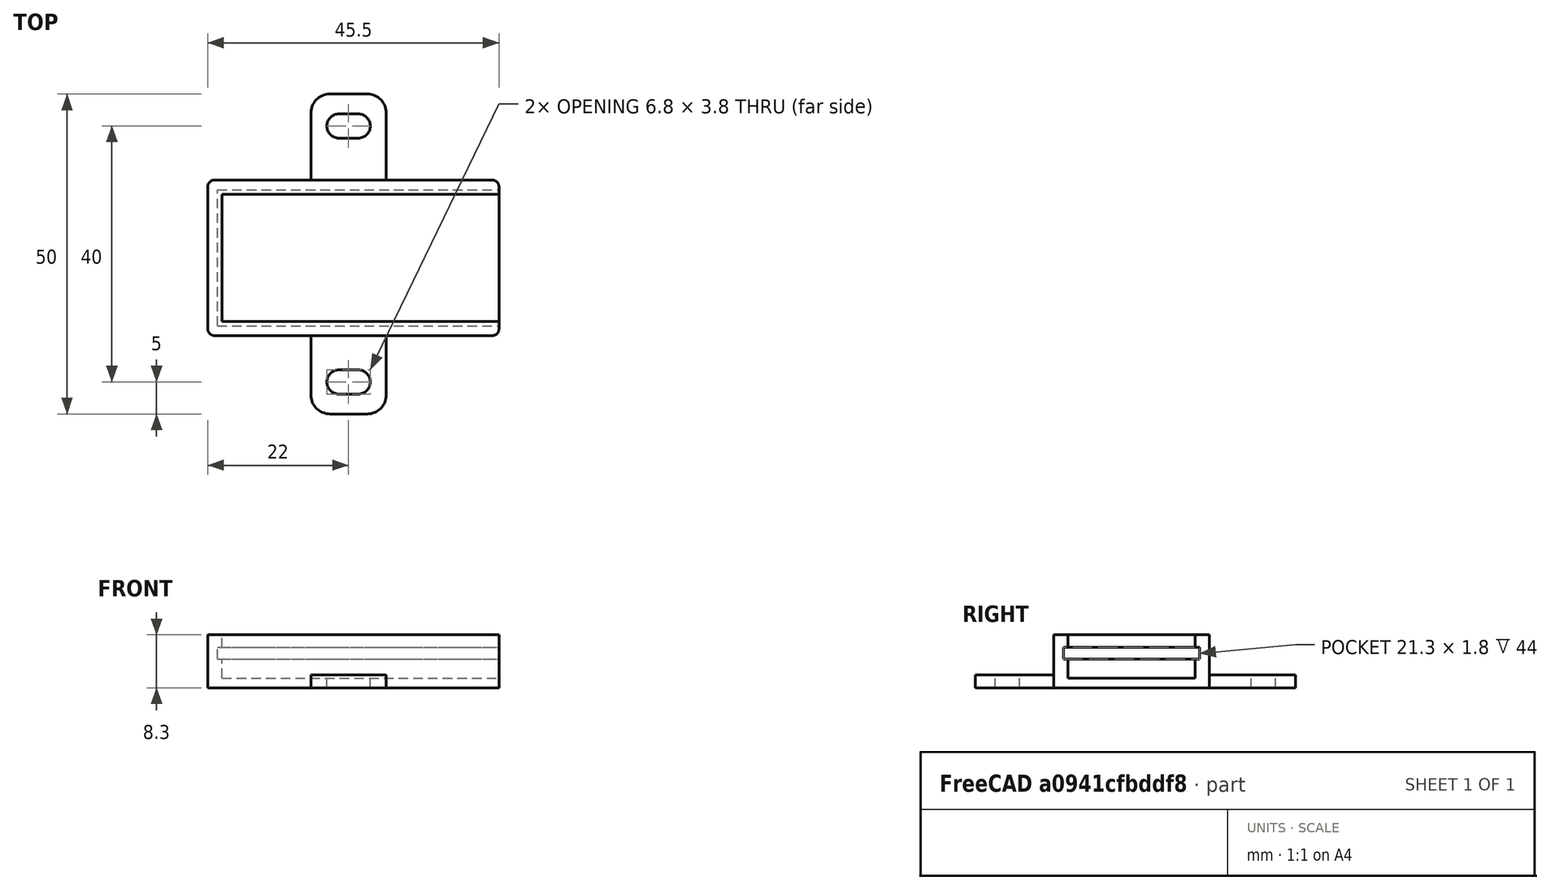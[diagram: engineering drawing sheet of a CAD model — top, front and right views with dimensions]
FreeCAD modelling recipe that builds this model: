
FCSTD DOCUMENT  (FreeCAD 0.19R)
Label: step_down_lm2596s_44x21
License: FreeArt
LicenseURL: http://artlibre.org/licence/lal
objects: Part::Box×3, Part::MultiFuse×2, Spreadsheet::Sheet×1, Part::Fillet×1, Part::Feature×1, Part::Cut×1, App::Part×1
note: 8 computed .brp shape members not serialized (recipe doc carries the construction recipe); baked Part::Feature solids carry a one-line shape summary decoded from their .brp

FEATURE [Spreadsheet::Sheet] Spreadsheet  label="p"
  cells = A1=pcb_x; B1(pcb_x)=44; A2=pcb_y; B2(pcb_y)=21.3; A3=pcb_z; B3(pcb_z)=1.8; A4=pcb_under; B4(pcb_under)=3; A5=side_wall; B5(side_wall)=1.5; A6=pcb_side_lane; B6(pcb_side_lane)=0.7; A7=bottom_wall; B7(bottom_wall)=1.5; A8=pcb_above; B8(pcb_above)=2
FEATURE [Part::Box] Box  label="external cube"
  AttacherType = Attacher::AttachEngine3D
  Height = 8.3
  Length = 45.5
  Width = 24.3
  expr: Length = <<p>>.pcb_x + <<p>>.side_wall
  expr: Width = <<p>>.pcb_y + 2 * <<p>>.side_wall
  expr: Height = <<p>>.bottom_wall + <<p>>.pcb_under + <<p>>.pcb_z + <<p>>.pcb_above
FEATURE [Part::Box] Box006  label="internal cube"
  AttacherType = Attacher::AttachEngine3D
  Height = 6.8
  Length = 44.1
  Placement = pos=(2.2,2.2,1.5) rot=(0,0,1;0rad)
  Width = 19.9
  expr: Length = <<p>>.pcb_x - 2 * <<p>>.pcb_side_lane + <<p>>.side_wall
  expr: Width = <<p>>.pcb_y - 2 * <<p>>.pcb_side_lane
  expr: Height = <<p>>.pcb_under + <<p>>.pcb_z + <<p>>.pcb_above
  expr: .Placement.Base.z = <<p>>.bottom_wall
  expr: .Placement.Base.x = <<p>>.side_wall + <<p>>.pcb_side_lane
  expr: .Placement.Base.y = <<p>>.side_wall + <<p>>.pcb_side_lane
FEATURE [Part::Box] Box007  label="pcb extract cube"
  AttacherType = Attacher::AttachEngine3D
  Height = 1.8
  Length = 44
  Placement = pos=(1.5,1.5,4.5) rot=(0,0,1;0rad)
  Width = 21.3
  expr: Height = <<p>>.pcb_z
  expr: .Placement.Base.z = <<p>>.bottom_wall + <<p>>.pcb_under
  expr: Width = <<p>>.pcb_y
  expr: Length = <<p>>.pcb_x
  expr: .Placement.Base.x = <<p>>.side_wall
  expr: .Placement.Base.y = <<p>>.side_wall
FEATURE [Part::MultiFuse] Fusion  label="extract fusion"
  Shapes = -> [Box006,Box007]
FEATURE [Part::Fillet] Fillet  label="external fillet"
  Base = -> Box
  Edges = 4 edges r=1: [Edge1,Edge3,Edge5,Edge7]
FEATURE [Part::Feature] Cut002002  label="attach plane y dir002"
  Placement = pos=(16.1,-12.25,0) rot=(0,0,1;0rad)
  shape: bbox 11.8 x 50 x 2 mm, 20 faces (baked)
FEATURE [Part::MultiFuse] Fusion001  label="solid fusion"
  Shapes = -> [Fillet,Cut002002]
FEATURE [Part::Cut] Cut  label="body cut"
  Base = -> Fusion001
  Tool = -> Fusion
FEATURE [App::Part] Part  label="lm2596s pcb box part"
  Group = -> [Box,Fillet,Fusion001,Fusion,Box007,Box006,Cut]
  Origin = -> Origin
